# Revit family: 2CKA006430A0403
name_source: partatom
category: Elektroinstallationen
revit_build: Autodesk Revit 2017 (Build: 20160225_1515(x64)
units: mm (PartAtom-declared; Revit-internal decimal feet)

## family parameters
Basisbauteil = Fläche
Beim Laden mit Abzugskörper schneiden = Nein
Bemaßung runder Anschluss = Durchmesser verwenden
Beschriftungsausrichtung beibehalten = Nein
Gemeinsam genutzt = Nein
Raumberechnungspunkt = Nein
Teiletyp = Normal

## types (1)
- 2CKA006430A0403
    Aufdruck/Kennzeichnung = Symbol "Pfeile"
    Ausführung = einteilige Taste
    Ausführung der Oberfläche = glänzend
    BIM = https://media.live.bim.site
    BIMSITE_PRODUCT_ID = 89742ae76b915595d154946b93d31de08d64aaac
    Befestigungsart = Klemmbefestigung
    Beschreibung = Bedienelement, alpinweiß, Busch-balance SI, Bedienelemente für Jalousiesteuerung/Zeitschaltuhren, Bedienelement Für Busch-Jalousiecontrol II Einsatz 6411 U-101, 6411 U/S-101. Für Jalousie-Basis-Einsatz 6418 U. Für Busch-Universal-Serieneinsatz 6402 U.
    Datenblatt = https://media.live.bim.site
    Farbe = weiß
    GTIN = 4011395191958
    Geeignet für Schutzart (IP) = IP20
    Gewicht [kg/m] = 0.028
    HAN = 2CKA006430A0403
    Halogenfrei = Ja
    HeinzeBIM = https://www.heinze.de
    Hersteller = Busch-Jaeger
    Ist System = Nein
    Ist Zubehör = Nein
    Kontrollfenster/Lichtauslass = Ja
    Oberfläche = unbehandelt
    Produktseite = https://media.live.bim.site
    RAL-Nummer (ähnlich) = 9010
    TYPE = 6430-914-102
    Typname = Bedienelement, alpinweiß, Busch-balance SI, Bedienelemente für Jalousiesteuerung/Zeitschaltuhren
    URL = https://www.busch-jaeger.de
    Verwendung = Jalousie
    Vorgabe-Ansicht = 1219 mm
    Werkstoff = Kunststoff
    Werkstoffgüte = Thermoplast

## geometry (parser evidence)
native form markers: Sweep x1
no freeform markers — native parametric forms only
